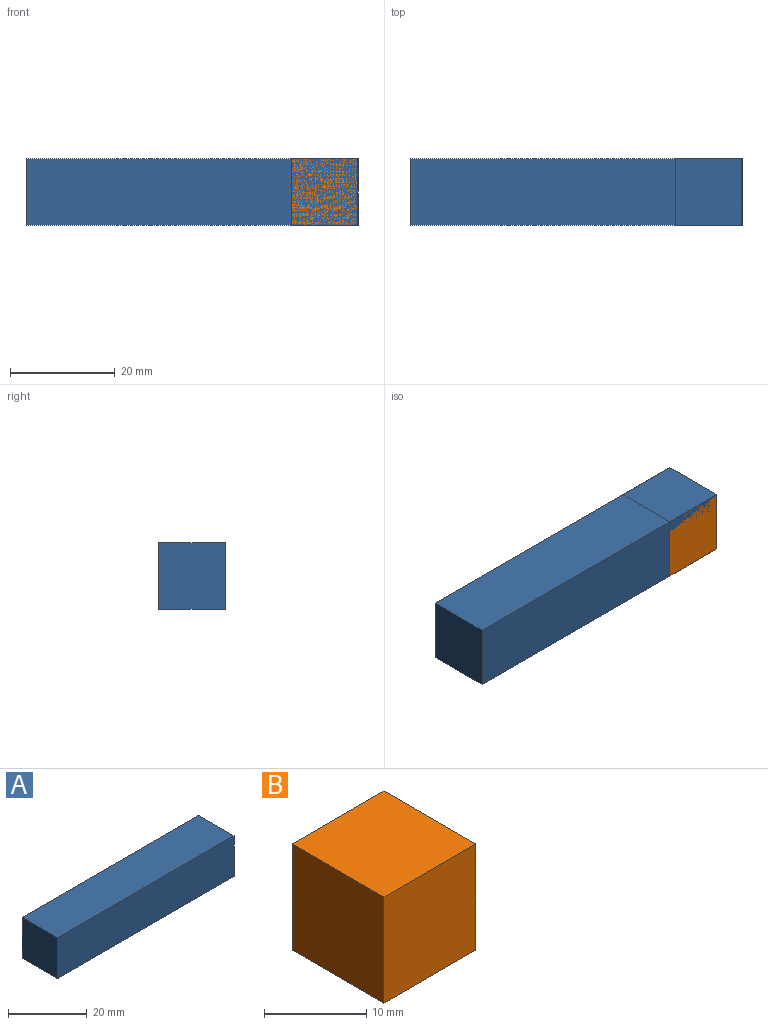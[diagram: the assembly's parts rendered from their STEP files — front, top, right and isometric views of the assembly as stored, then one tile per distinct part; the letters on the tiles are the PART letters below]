
ASSEMBLY  parts=2 mates=1
PART A: 6 faces, bbox 63.5x12.7x12.7 mm
  f0: plane 63.5x12.7mm, normal (0,0,-1), area 806.5mm2, adj f1,f3,f4,f5
  f1: plane 12.7x12.7mm, normal (1,0,0), area 161.3mm2, adj f0,f2,f4,f5
  f2: plane 63.5x12.7mm, normal (0,0,1), area 806.5mm2, adj f1,f3,f4,f5
  f3: plane 12.7x12.7mm, normal (-1,0,0), area 161.3mm2, adj f0,f2,f4,f5
  f4: plane 63.5x12.7mm, normal (0,-1,0), area 806.5mm2, adj f0,f1,f2,f3
  f5: plane 63.5x12.7mm, normal (0,1,0), area 806.5mm2, adj f0,f1,f2,f3
PART B: 6 faces, bbox 12.7x12.7x12.7 mm
  f0: plane 12.7x12.7mm, normal (0,0,-1), area 161.3mm2, adj f1,f3,f4,f5
  f1: plane 12.7x12.7mm, normal (1,0,0), area 161.3mm2, adj f0,f2,f4,f5
  f2: plane 12.7x12.7mm, normal (0,0,1), area 161.3mm2, adj f1,f3,f4,f5
  f3: plane 12.7x12.7mm, normal (-1,0,0), area 161.3mm2, adj f0,f2,f4,f5
  f4: plane 12.7x12.7mm, normal (0,-1,0), area 161.3mm2, adj f0,f1,f2,f3
  f5: plane 12.7x12.7mm, normal (0,1,0), area 161.3mm2, adj f0,f1,f2,f3
PLACE A t=(17.72,38.38,52.81)mm
PLACE B t=(39.81,38.38,-19.37)mm
MATE slider B.f1 <-> A.f1  axis (1,0,0) through (46.16,32.03,9.2)mm
